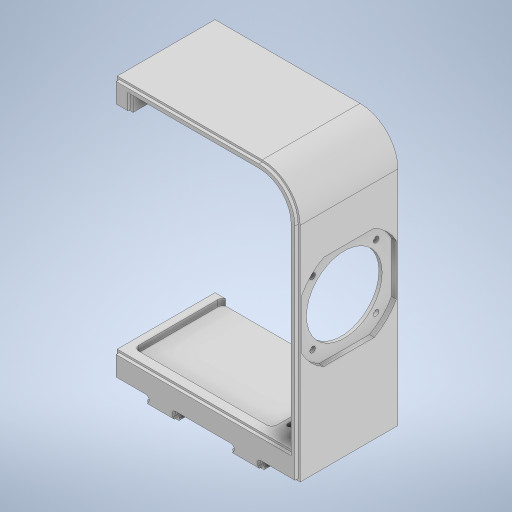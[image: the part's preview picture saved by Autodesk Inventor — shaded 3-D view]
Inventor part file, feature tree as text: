
AUTODESK INVENTOR PART (.ipt)
format: ipt  version: 2023 (Build 270158000, 158)  size: 532,992 bytes
history: native  units: in
note: dims shown in document units (in); Inventor stores cm internally (conversion verified against a paired STEP export)
features: extrude x13, sketch x12, projected_geometry x7, shell x1, fillet x1
ambient origin geometry x8: Origin, YZ Plane, XZ Plane, XY Plane, X Axis, Y Axis, Z Axis, Center Point
bodies: Solid1 (feature_tree)
feature tree (34):
  extrude  "Extrusion1"  Depth=6.4961in
  shell  "Shell2"  Thickness=6.4961in
  sketch  "Sketch6"  dims[d3=2.4409in d4=0.0in d29=0.1969in]
  sketch  "Sketch7"  dims[d38=0.3937in d39=0.3937in]
  extrude  "Extrusion6"  Depth=0.1969in
  extrude  "Extrusion7"  Depth=0.3937in
  extrude  "Extrusion8"  Depth=0.3937in
  extrude  "Extrusion9"  Depth=0.3937in TaperAngle=0.0deg
  extrude  "Extrusion11"  Depth=0.3937in
  extrude  "Extrusion12"  Depth=0.1181in
  fillet  "Fillet4"  Radius=0.1181in
  extrude  "Extrusion13"  Depth=0.1181in
  extrude  "Extrusion14"  Depth=0.1181in
  sketch  "Sketch17"  dims[d56=0.1969in d57=0.0118in]
  extrude  "Extrusion15"  Depth=0.1969in
  extrude  "Extrusion16"  Depth=0.0787in TaperAngle=0.0deg
  extrude  "Extrusion17"  Depth=0.3937in TaperAngle=0.0deg
  extrude  "Extrusion18"  Depth=0.0394in
  sketch  "Sketch1"  dims[d0=0.9449in d1=3.622in d2=6.4961in]
  projected_geometry  "Projected Loop1"
  sketch  "Sketch9"  dims[d40=0.3937in d41=0.3937in]
  projected_geometry  "Projected Loop2"
  sketch  "Sketch10"  dims[d42=0.3937in d43=0.0in d44=0.3937in d45=0.0in]
  sketch  "Sketch12"  dims[d46=0.3937in d47=0.0in d48=3.189in]
  projected_geometry  "Projected Loop4"
  sketch  "Sketch14"  dims[d49=0.1181in d50=1.9685in d51=0.1181in]
  projected_geometry  "Projected Loop5"
  sketch  "Sketch15"  dims[d52=3.189in d53=0.1181in]
  projected_geometry  "Projected Loop6"
  sketch  "Sketch16"  dims[d54=1.9685in d55=0.1181in]
  projected_geometry  "Projected Loop7"
  sketch  "Sketch18"  dims[d58=0.1575in d59=0.0in d63=0.0787in d64=0.0in]
  sketch  "Sketch19"  dims[d70=0.1969in d71=45.0deg d72=45.0deg d73=45.0deg d74=0.7874in d75=0.9843in d76=0.9843in d77=0.7874in d78=4.685in d79=0.0118in d80=0.0118in d81=0.0118in d82=0.0118in d83=0.0118in d84=0.0118in d85=4.685in d86=0.3937in d87=0.0in d88=0.0394in d89=0.0512in d90=0.0787in d91=0.0in d92=0.7087in d93=0.1181in d95=0.5118in d96=0.0in d97=0.0in d98=0.7087in d100=1.5748in d101=2.3622in d102=2.3622in d103=2.6772in d104=1.8504in d105=0.315in d106=1.122in d107=0.1417in d108=1.8898in d109=360.0deg d110=2.7559in d111=2.7559in d114=0.7874in d115=0.1181in d116=0.0in d117=0.0in d118=0.0in d119=0.0394in d120=0.1417in d121=0.1181in d122=0.1969in d123=0.3937in d124=0.1417in d125=0.1417in d126=0.5906in d127=0.1575in d128=0.1575in d129=0.1969in d130=0.1969in d131=0.3937in d132=0.0in d133=0.1417in d134=0.1417in d135=0.1417in d136=0.1417in d137=0.1969in d138=0.1969in d139=0.1969in d140=0.1969in d141=0.1969in d142=0.2559in d143=0.1969in d144=0.2559in d145=0.3937in d146=0.0in]
  projected_geometry  "Projected Loop8"
